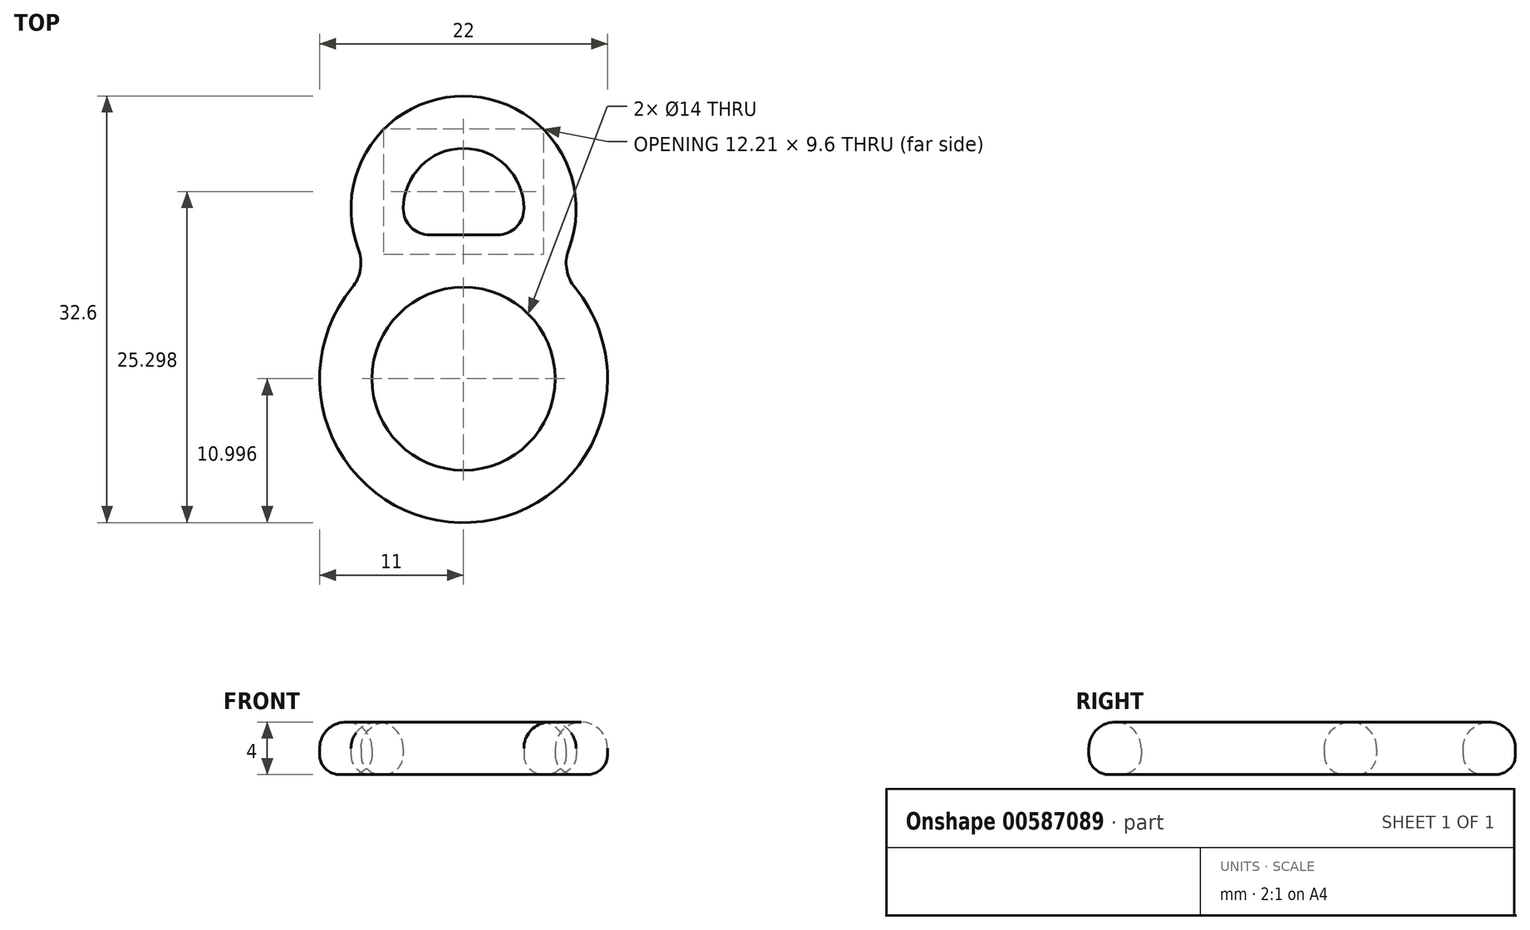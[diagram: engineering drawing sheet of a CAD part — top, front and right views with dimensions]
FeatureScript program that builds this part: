
annotation { "Feature Type Name" : "Feature", "Feature Type Description" : "" }
export const myFeature = defineFeature(function(context is Context, id is Id, definition is map)
    precondition{}
    {
        {
            var Q0;
            Q0=qCreatedBy(makeId("Top.planeOp"),FACE);
            var sketch = newSketch(context, id + "F0", { "sketchPlane" : qUnion([Q0])});
            skLineSegment(sketch, "E0", {"start": v(-2.6, -0.72) * mm, "end": v(2.6, -0.72) * mm});
            skLineSegment(sketch, "E1", {"start": v(-5.01, -4.72) * mm, "end": v(3.48, -4.72) * mm, "construction": true});
            skArc(sketch, "E2", {"start": v(4.6, 1.28) * mm, "mid": v(0, 5.88) * mm, "end": v(-4.6, 1.28) * mm});
            skArc(sketch, "E3.0", {"start": v(8.04, -1.8) * mm, "mid": v(0, 9.88) * mm, "end": v(-8.04, -1.8) * mm});
            skPoint(sketch, "E4.visualSharp", {"position": v(-4.15, -0.72) * mm});
            skArc(sketch, "E4.filletArc", {"start": v(-4.6, 1.28) * mm, "mid": v(-4.02, -0.14) * mm, "end": v(-2.6, -0.72) * mm});
            skPoint(sketch, "E5.visualSharp", {"position": v(4.15, -0.72) * mm});
            skArc(sketch, "E5.filletArc", {"start": v(2.6, -0.72) * mm, "mid": v(4.02, -0.14) * mm, "end": v(4.6, 1.28) * mm});
            skLineSegment(sketch, "E6", {"start": v(-5.01, -4.72) * mm, "end": v(-11.32, -4.72) * mm, "construction": true});
            skLineSegment(sketch, "E7", {"start": v(3.48, -4.72) * mm, "end": v(11.27, -4.72) * mm, "construction": true});
            skLineSegment(sketch, "E8", {"start": v(0, 0) * mm, "end": v(0, -14.2) * mm, "construction": true});
            skCircle(sketch, "E9", {"center": v(0, -11.72) * mm, "radius": 7 * mm});
            skArc(sketch, "E10.0", {"start": v(-8.52, -4.76) * mm, "mid": v(0, -22.72) * mm, "end": v(8.52, -4.76) * mm});
            skPoint(sketch, "E11.visualSharp", {"position": v(-7.21, -3.42) * mm});
            skArc(sketch, "E11.filletArc", {"start": v(-8.52, -4.76) * mm, "mid": v(-7.88, -3.34) * mm, "end": v(-8.04, -1.8) * mm});
            skPoint(sketch, "E12.visualSharp", {"position": v(7.21, -3.42) * mm});
            skArc(sketch, "E12.filletArc", {"start": v(8.04, -1.8) * mm, "mid": v(7.88, -3.34) * mm, "end": v(8.52, -4.76) * mm});
            skSolve(sketch);
        }
        {
            var Q0;
            Q0 = qSketchRegion(id + "F0", true);
            extrude(context, id + "F1", {"entities" : qUnion([Q0]), "depth" : 4 * mm, "offsetDistance" : 25 * mm});
        }
        {
            var Q0;
            Q0=makeQuery(id+"F1.opExtrude","CAP_EDGE",EDGE,{"disambiguationData":[OSD([sQuery(id+"F0.wireOp",EDGE,"E2")])],"isStart":false});
            var Q1;
            Q1=makeQuery(id+"F1.opExtrude","CAP_EDGE",EDGE,{"disambiguationData":[OSD([sQuery(id+"F0.wireOp",EDGE,"E4.filletArc")])],"isStart":false});
            var Q2;
            Q2=makeQuery(id+"F1.opExtrude","CAP_EDGE",EDGE,{"disambiguationData":[OSD([sQuery(id+"F0.wireOp",EDGE,"E0")])],"isStart":false});
            var Q3;
            Q3=makeQuery(id+"F1.opExtrude","CAP_EDGE",EDGE,{"disambiguationData":[OSD([sQuery(id+"F0.wireOp",EDGE,"E5.filletArc")])],"isStart":false});
            var Q4;
            Q4=makeQuery(id+"F1.opExtrude","CAP_EDGE",EDGE,{"disambiguationData":[OSD([sQuery(id+"F0.wireOp",EDGE,"49cf1c97-2c96-48e2-837b-f6d187fe493c.filletArc")])],"isStart":false});
            var Q5;
            Q5=makeQuery(id+"F1.opExtrude","CAP_EDGE",EDGE,{"disambiguationData":[OSD([sQuery(id+"F0.wireOp",EDGE,"E9")])],"isStart":false});
            var Q6;
            Q6=makeQuery(id+"F1.opExtrude","CAP_EDGE",EDGE,{"disambiguationData":[OSD([sQuery(id+"F0.wireOp",EDGE,"E10.0")])],"isStart":false});
            fillet(context, id + "F2", {"entities" : qUnion([Q0, Q1, Q2, Q3, Q4, Q5, Q6]), "radius" : 2 * mm, "tangentPropagation" : true, "allowEdgeOverflow" : false});
        }
        {
            var Q0;
            Q0=makeQuery(id+"F1.opExtrude","CAP_EDGE",EDGE,{"disambiguationData":[OSD([sQuery(id+"F0.wireOp",EDGE,"E9")])],"isStart":true});
            var Q1;
            Q1=makeQuery(id+"F1.opExtrude","CAP_EDGE",EDGE,{"disambiguationData":[OSD([sQuery(id+"F0.wireOp",EDGE,"E2")])],"isStart":true});
            var Q2;
            Q2=makeQuery(id+"F1.opExtrude","CAP_EDGE",EDGE,{"disambiguationData":[OSD([sQuery(id+"F0.wireOp",EDGE,"E10.0")])],"isStart":true});
            fillet(context, id + "F3", {"entities" : qUnion([Q0, Q1, Q2]), "radius" : 1.5 * mm, "tangentPropagation" : true, "allowEdgeOverflow" : false});
        }
    });
